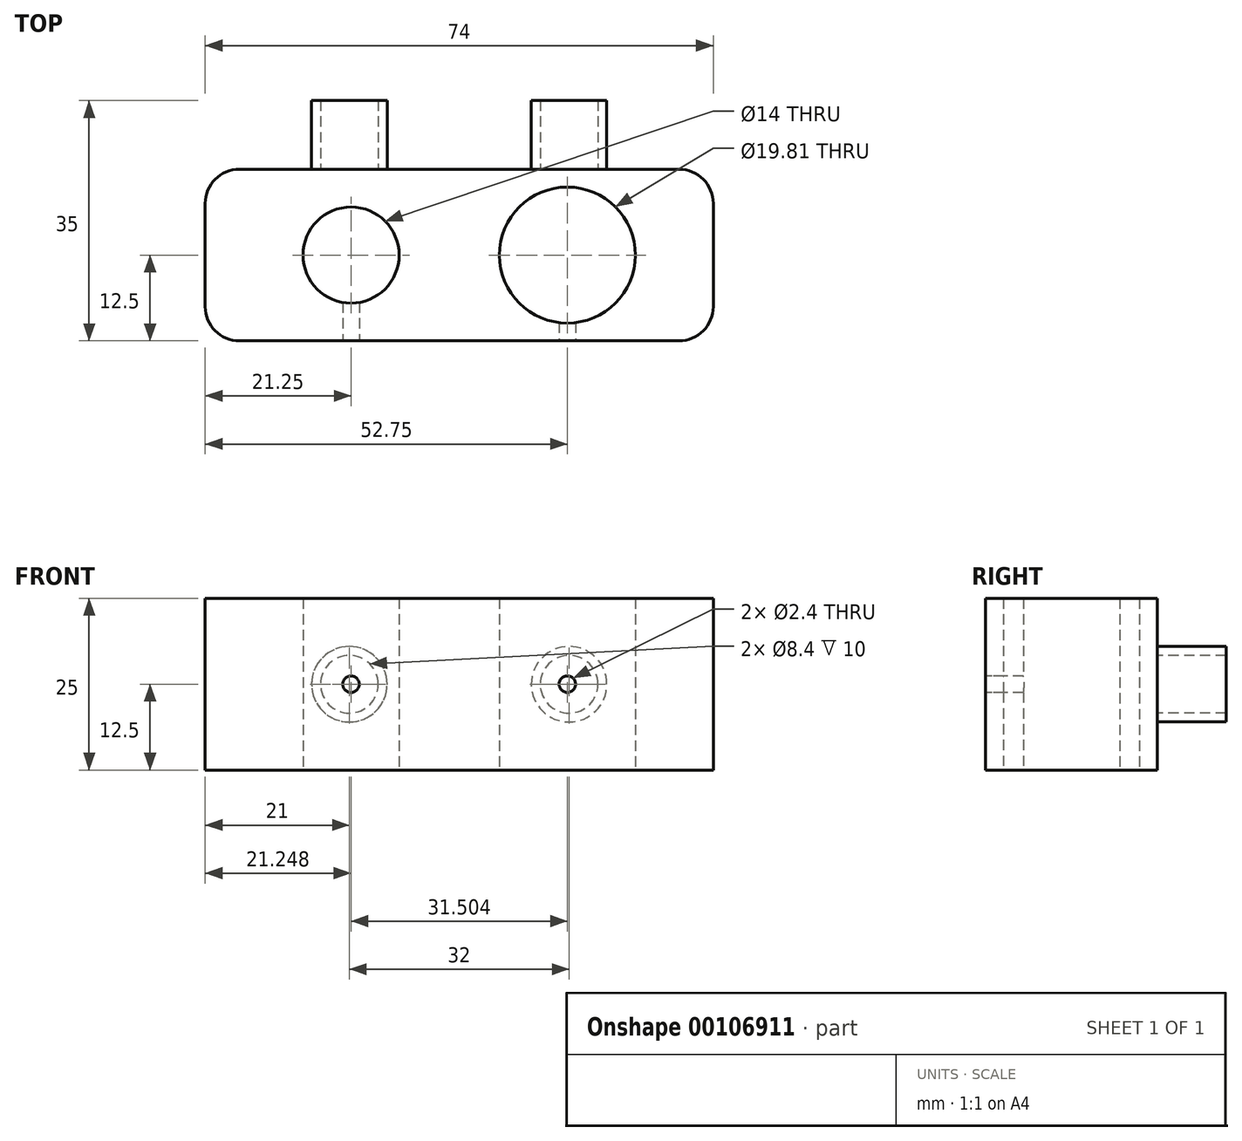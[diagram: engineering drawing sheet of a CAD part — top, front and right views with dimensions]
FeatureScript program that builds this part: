
annotation { "Feature Type Name" : "Feature", "Feature Type Description" : "" }
export const myFeature = defineFeature(function(context is Context, id is Id, definition is map)
    precondition{}
    {
        {
            var Q0;
            Q0=qCreatedBy(makeId("Top.planeOp"),FACE);
            var sketch = newSketch(context, id + "F0", { "sketchPlane" : qUnion([Q0])});
            skLineSegment(sketch, "E0.bottom", {"start": v(37, -12.5) * mm, "end": v(-37, -12.5) * mm});
            skLineSegment(sketch, "E0.top", {"start": v(37, 12.5) * mm, "end": v(-37, 12.5) * mm});
            skLineSegment(sketch, "E0.left", {"start": v(37, -12.5) * mm, "end": v(37, 12.5) * mm});
            skLineSegment(sketch, "E0.right", {"start": v(-37, -12.5) * mm, "end": v(-37, 12.5) * mm});
            skPoint(sketch, "E0.middle", {"position": v(0, 0) * mm});
            skCircle(sketch, "E1", {"center": v(-15.75, 0) * mm, "radius": 7 * mm});
            skCircle(sketch, "E2", {"center": v(15.75, 0) * mm, "radius": 9.9 * mm});
            skSolve(sketch);
        }
        {
            var Q0;
            Q0=makeQuery(id+"F0.imprint","IMPRINT",FACE,{"disambiguationData":[TD([[makeQuery(id+"F0.imprint","IMPRINT",EDGE,{"derivedFrom":sQuery(id+"F0.wireOp",EDGE,"E0.bottom")}),-1.0]])]});
            extrude(context, id + "F1", {"entities" : qUnion([Q0]), "depth" : 25 * mm});
        }
        {
            var Q0;
            Q0=makeQuery(id+"F1.opExtrude","SWEPT_FACE",FACE,{"disambiguationData":[OSD([sQuery(id+"F0.wireOp",EDGE,"E0.bottom")])]});
            var sketch = newSketch(context, id + "F2", { "sketchPlane" : qUnion([Q0])});
            skLineSegment(sketch, "E3", {"start": v(37, 25) * mm, "end": v(25.66, 25) * mm, "construction": true});
            skLineSegment(sketch, "E4", {"start": v(25.66, 25) * mm, "end": v(25.66, 0) * mm, "construction": true});
            skLineSegment(sketch, "E5", {"start": v(25.66, 0) * mm, "end": v(37, 0) * mm, "construction": true});
            skLineSegment(sketch, "E6", {"start": v(0, 25) * mm, "end": v(5.84, 25) * mm, "construction": true});
            skLineSegment(sketch, "E7", {"start": v(5.84, 25) * mm, "end": v(5.84, 0) * mm, "construction": true});
            skLineSegment(sketch, "E8", {"start": v(5.84, 0) * mm, "end": v(0, 0) * mm, "construction": true});
            skLineSegment(sketch, "E9", {"start": v(5.84, 25) * mm, "end": v(25.66, 0) * mm, "construction": true});
            skLineSegment(sketch, "E10", {"start": v(5.84, 0) * mm, "end": v(25.66, 25) * mm, "construction": true});
            skPoint(sketch, "E11", {"position": v(15.75, 12.5) * mm});
            skPoint(sketch, "E12.MirrorP", {"position": v(-15.75, 12.5) * mm});
            skSolve(sketch);
        }
        {
            var Q0;
            Q0=sQuery(id+"F2.wireOp",VERTEX,"E11");
            var Q1;
            Q1=sQuery(id+"F2.wireOp",VERTEX,"E12.MirrorP");
            var Q2;
            Q2=makeQuery(id+"F1.opExtrude","SWEPT_BODY",BODY,{"disambiguationData":[OSD([sQuery(id+"F0.wireOp",EDGE,"E0.bottom"),sQuery(id+"F0.wireOp",EDGE,"E0.top"),sQuery(id+"F0.wireOp",EDGE,"E0.left"),sQuery(id+"F0.wireOp",EDGE,"E0.right"),sQuery(id+"F0.wireOp",EDGE,"E1"),sQuery(id+"F0.wireOp",EDGE,"E2")])]});
            hole(context, id + "F3", {"style" : HoleStyle.SIMPLE, "endStyle" : HoleEndStyle.BLIND, "standardTappedOrClearance" : lookupTablePath({ "standard" : "ISO", "engagement" : "75%", "pitch" : "0.6 mm", "size" : "M3", "type" : "Tapped" }), "standardBlindInLast" : lookupTablePath({ "standard" : "ISO", "engagement" : "75%", "pitch" : "0.6 mm", "size" : "M3", "type" : "Tapped" }), "holeDiameter" : 2.4 * mm, "holeDepth" : 10 * mm, "locations" : qUnion([Q0, Q1]), "scope" : qUnion([Q2])});
        }
        {
            var Q0;
            Q0=makeQuery(id+"F1.opExtrude","SWEPT_EDGE",EDGE,{"disambiguationData":[OSD([sQuery(id+"F0.wireOp",EDGE,"E0.bottom"),sQuery(id+"F0.wireOp",EDGE,"E0.right")])]});
            var Q1;
            Q1=makeQuery(id+"F1.opExtrude","SWEPT_EDGE",EDGE,{"disambiguationData":[OSD([sQuery(id+"F0.wireOp",EDGE,"E0.bottom"),sQuery(id+"F0.wireOp",EDGE,"E0.left")])]});
            var Q2;
            Q2=makeQuery(id+"F1.opExtrude","SWEPT_EDGE",EDGE,{"disambiguationData":[OSD([sQuery(id+"F0.wireOp",EDGE,"E0.top"),sQuery(id+"F0.wireOp",EDGE,"E0.left")])]});
            var Q3;
            Q3=makeQuery(id+"F1.opExtrude","SWEPT_EDGE",EDGE,{"disambiguationData":[OSD([sQuery(id+"F0.wireOp",EDGE,"E0.top"),sQuery(id+"F0.wireOp",EDGE,"E0.right")])]});
            fillet(context, id + "F4", {"entities" : qUnion([Q0, Q1, Q2, Q3]), "radius" : 5 * mm, "tangentPropagation" : true, "allowEdgeOverflow" : false});
        }
        {
            var Q0;
            Q0=makeQuery(id+"F1.opExtrude","SWEPT_FACE",FACE,{"disambiguationData":[OSD([sQuery(id+"F0.wireOp",EDGE,"E0.top")])]});
            var sketch = newSketch(context, id + "F5", { "sketchPlane" : qUnion([Q0])});
            skLineSegment(sketch, "E13", {"start": v(-32, 25) * mm, "end": v(0, 0) * mm, "construction": true});
            skLineSegment(sketch, "E14", {"start": v(0, 0) * mm, "end": v(32, 25) * mm, "construction": true});
            skLineSegment(sketch, "E15", {"start": v(-32, 0) * mm, "end": v(0, 25) * mm, "construction": true});
            skLineSegment(sketch, "E16", {"start": v(0, 25) * mm, "end": v(32, 0) * mm, "construction": true});
            skCircle(sketch, "E17", {"center": v(-16, 12.5) * mm, "radius": 5.5 * mm});
            skCircle(sketch, "E18", {"center": v(16, 12.5) * mm, "radius": 5.5 * mm});
            skCircle(sketch, "E19", {"center": v(-16, 12.5) * mm, "radius": 4.2 * mm});
            skCircle(sketch, "E20", {"center": v(16, 12.5) * mm, "radius": 4.2 * mm});
            skSolve(sketch);
        }
        {
            var Q0;
            Q0 = qSketchRegion(id + "F5", true);
            extrude(context, id + "F6", {"entities" : qUnion([Q0]), "operationType" : NewBodyOperationType.ADD, "depth" : 10 * mm});
        }
    });
